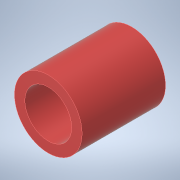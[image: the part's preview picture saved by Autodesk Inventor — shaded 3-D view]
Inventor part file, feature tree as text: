
AUTODESK INVENTOR PART (.ipt)
format: ipt  version: 2022.3 (Build 263350000, 350)  size: 107,008 bytes
history: native  units: in
note: dims shown in document units (in); Inventor stores cm internally (conversion verified against a paired STEP export)
features: sketch x1, extrude x1
ambient origin geometry x8: Origin, YZ Plane, XZ Plane, XY Plane, X Axis, Y Axis, Z Axis, Center Point
bodies: Solid1 (feature_tree)
feature tree (2):
  sketch  "Sketch1"  dims[d1=1.0in d2=0.0in d13=0.561in d14=0.125in]
  extrude  "Extrusion1"  TaperAngle=0.0deg  [1 undecoded]
note: 1 required parameter value undecoded (feature->parameter linkage not recoverable at this tier; creation-order binding heuristic only, values carry confidence <= 0.55)
